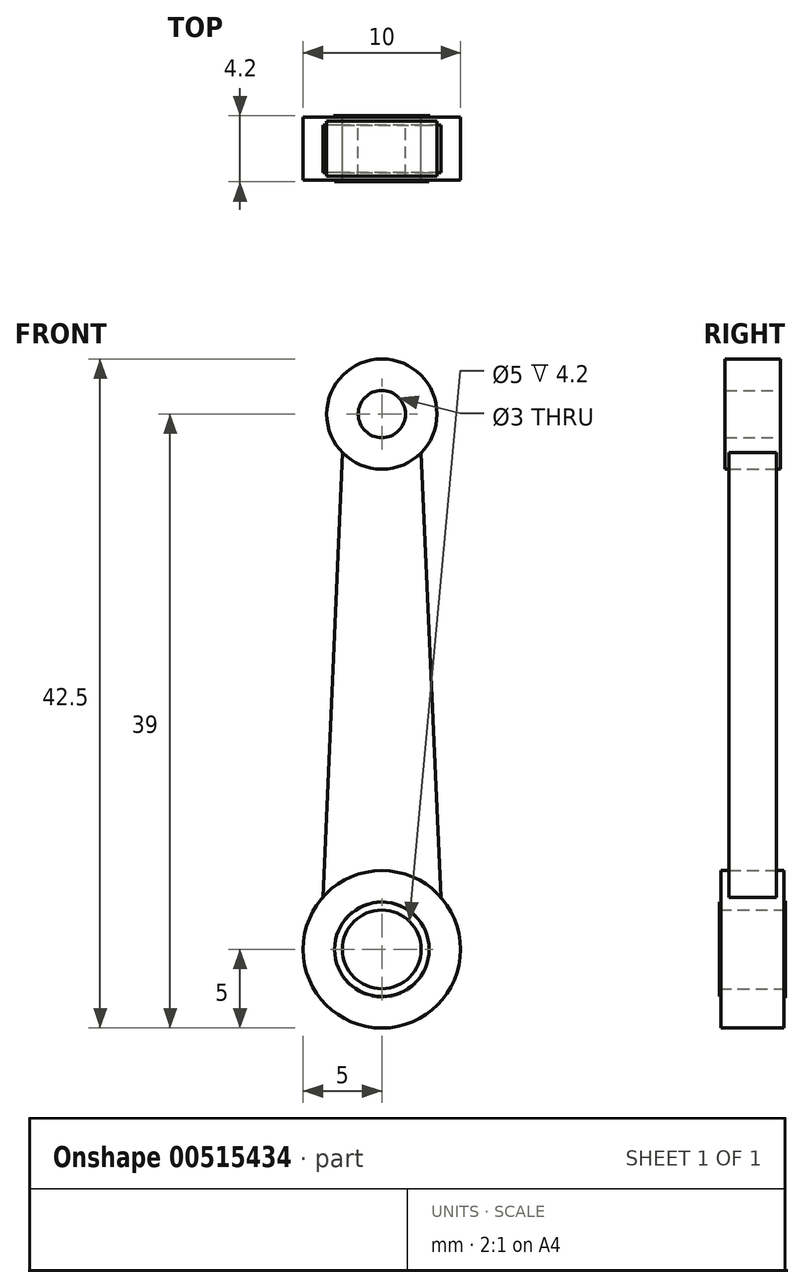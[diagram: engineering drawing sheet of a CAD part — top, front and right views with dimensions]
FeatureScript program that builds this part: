
annotation { "Feature Type Name" : "Feature", "Feature Type Description" : "" }
export const myFeature = defineFeature(function(context is Context, id is Id, definition is map)
    precondition{}
    {
        {
            var Q0;
            Q0=qCreatedBy(makeId("Front.planeOp"),FACE);
            var sketch = newSketch(context, id + "F0", { "sketchPlane" : qUnion([Q0])});
            skCircle(sketch, "E0", {"center": v(0, 0) * mm, "radius": 5 * mm});
            skCircle(sketch, "E1", {"center": v(0, 0) * mm, "radius": 3.25 * mm});
            skCircle(sketch, "E2", {"center": v(0, 0) * mm, "radius": 2.5 * mm});
            skLineSegment(sketch, "E3", {"start": v(0, 40.04) * mm, "end": v(0, -5.64) * mm, "construction": true});
            skPoint(sketch, "E4", {"position": v(0, 34) * mm});
            skCircle(sketch, "E5", {"center": v(0, 34) * mm, "radius": 3.5 * mm});
            skCircle(sketch, "E6", {"center": v(0, 34) * mm, "radius": 1.5 * mm});
            skLineSegment(sketch, "E7", {"start": v(-2.5, 31.55) * mm, "end": v(2.5, 31.55) * mm, "construction": true});
            skLineSegment(sketch, "E8", {"start": v(-3.75, 3.3) * mm, "end": v(3.75, 3.3) * mm, "construction": true});
            skPoint(sketch, "E9", {"position": v(0, 31.55) * mm});
            skPoint(sketch, "E10", {"position": v(0, 3.3) * mm});
            skLineSegment(sketch, "E11", {"start": v(-2.5, 31.55) * mm, "end": v(-3.75, 3.3) * mm});
            skLineSegment(sketch, "E12", {"start": v(2.5, 31.55) * mm, "end": v(3.75, 3.3) * mm});
            skSolve(sketch);
        }
        {
            var Q0;
            Q0=makeQuery(id+"F0.imprint","IMPRINT",FACE,{"disambiguationData":[TD([[makeQuery(id+"F0.imprint","IMPRINT",EDGE,{"derivedFrom":sQuery(id+"F0.wireOp",EDGE,"E6")}),-1.0]])]});
            extrude(context, id + "F1", {"entities" : qUnion([Q0]), "endBound" : BoundingType.SYMMETRIC, "depth" : 3.5 * mm, "offsetDistance" : 25 * mm});
        }
        {
            var Q0;
            Q0=makeQuery(id+"F0.imprint","IMPRINT",FACE,{"disambiguationData":[TD([[makeQuery(id+"F0.imprint","IMPRINT",EDGE,{"derivedFrom":sQuery(id+"F0.wireOp",EDGE,"E1")}),-1.0]])]});
            extrude(context, id + "F2", {"entities" : qUnion([Q0]), "endBound" : BoundingType.SYMMETRIC, "depth" : 4 * mm, "offsetDistance" : 25 * mm});
        }
        {
            var Q0;
            Q0=makeQuery(id+"F0.imprint","IMPRINT",FACE,{"disambiguationData":[TD([[makeQuery(id+"F0.imprint","IMPRINT",EDGE,{"derivedFrom":sQuery(id+"F0.wireOp",EDGE,"E1")}),1.0]])]});
            extrude(context, id + "F3", {"entities" : qUnion([Q0]), "operationType" : NewBodyOperationType.ADD, "endBound" : BoundingType.SYMMETRIC, "depth" : 4 * mm, "offsetDistance" : 25 * mm});
        }
        {
            var Q0;
            {var subQ0=sQuery(id+"F0.wireOp",EDGE,"E11");Q0=makeQuery(id+"F0.imprint","IMPRINT",FACE,{"disambiguationData":[TD([[makeQuery(id+"F0.imprint","IMPRINT",EDGE,{"derivedFrom":subQ0}),1.0]])]});}
            extrude(context, id + "F4", {"entities" : qUnion([Q0]), "endBound" : BoundingType.SYMMETRIC, "depth" : 3 * mm, "offsetDistance" : 25 * mm});
        }
        {
            var Q0;
            Q0=qCreatedBy(makeId("Front.planeOp"),FACE);
            var sketch = newSketch(context, id + "F5", { "sketchPlane" : qUnion([Q0])});
            skCircle(sketch, "E13", {"center": v(0, 0) * mm, "radius": 3 * mm});
            skSolve(sketch);
        }
        {
            var Q0;
            {var subQ0=sQuery(id+"F0.wireOp",EDGE,"E1");Q0=makeQuery(id+"F3.boolean.opBoolean","MERGE",FACE,{"derivedFrom":[makeQuery(id+"F2.opExtrude","CAP_FACE",FACE,{"disambiguationData":[OSD([sQuery(id+"F0.wireOp",EDGE,"E0"),subQ0])],"isStart":false}),makeQuery(id+"F3.opExtrude","CAP_FACE",FACE,{"disambiguationData":[OSD([subQ0,sQuery(id+"F0.wireOp",EDGE,"E2")])],"isStart":false})]});}
            cPlane(context, id + "F6", {"entities" : qUnion([Q0]), "cplaneType" : CPlaneType.OFFSET, "offset" : 0 * mm, "width" : 150 * mm, "height" : 150 * mm});
        }
        {
            var Q0;
            Q0=qCreatedBy(id+"F6.planeOp",FACE);
            var sketch = newSketch(context, id + "F7", { "sketchPlane" : qUnion([Q0])});
            skCircle(sketch, "E14", {"center": v(0, 0) * mm, "radius": 3 * mm});
            skSolve(sketch);
        }
        {
            var Q0;
            {var subQ0=sQuery(id+"F0.wireOp",EDGE,"E1");Q0=makeQuery(id+"F3.boolean.opBoolean","MERGE",FACE,{"derivedFrom":[makeQuery(id+"F2.opExtrude","CAP_FACE",FACE,{"disambiguationData":[OSD([sQuery(id+"F0.wireOp",EDGE,"E0"),subQ0])],"isStart":true}),makeQuery(id+"F3.opExtrude","CAP_FACE",FACE,{"disambiguationData":[OSD([subQ0,sQuery(id+"F0.wireOp",EDGE,"E2")])],"isStart":true})]});}
            cPlane(context, id + "F8", {"entities" : qUnion([Q0]), "cplaneType" : CPlaneType.OFFSET, "offset" : 0 * mm, "width" : 150 * mm, "height" : 150 * mm});
        }
        {
            var Q0;
            Q0=qCreatedBy(id+"F8.planeOp",FACE);
            var sketch = newSketch(context, id + "F9", { "sketchPlane" : qUnion([Q0])});
            skCircle(sketch, "E15", {"center": v(0, 0) * mm, "radius": 3.07 * mm});
            skSolve(sketch);
        }
        {
            var Q0;
            Q0=makeQuery(id+"F7.imprint","IMPRINT",FACE,{"disambiguationData":[TD([[makeQuery(id+"F7.imprint","IMPRINT",EDGE,{"derivedFrom":sQuery(id+"F7.wireOp",EDGE,"E14")}),1.0]])]});
            extrude(context, id + "F10", {"entities" : qUnion([Q0]), "operationType" : NewBodyOperationType.ADD, "depth" : 0.1 * mm, "offsetDistance" : 25 * mm});
        }
        {
            var Q0;
            Q0=makeQuery(id+"F9.imprint","IMPRINT",FACE,{"disambiguationData":[TD([[makeQuery(id+"F9.imprint","IMPRINT",EDGE,{"derivedFrom":sQuery(id+"F9.wireOp",EDGE,"E15")}),1.0]])]});
            extrude(context, id + "F11", {"entities" : qUnion([Q0]), "operationType" : NewBodyOperationType.ADD, "depth" : 0.1 * mm, "offsetDistance" : 25 * mm});
        }
        {
            var Q0;
            Q0=sQuery(id+"F5.wireOp",VERTEX,"E13.center");
            var Q1;
            Q1=makeQuery(id+"F2.opExtrude","SWEPT_BODY",BODY,{"disambiguationData":[OSD([sQuery(id+"F0.wireOp",EDGE,"E0"),sQuery(id+"F0.wireOp",EDGE,"E1")])]});
            hole(context, id + "F12", {"style" : HoleStyle.SIMPLE, "endStyle" : HoleEndStyle.BLIND, "oppositeDirection" : true, "holeDiameter" : 5 * mm, "holeDepth" : 5 * mm, "isTappedThrough" : true, "tappedDepth" : 12 * mm, "tapClearance" : 3, "startFromSketch" : true, "locations" : qUnion([Q0]), "scope" : qUnion([Q1])});
        }
        {
            var Q0;
            Q0=qCreatedBy(id+"F8.planeOp",FACE);
            var sketch = newSketch(context, id + "F13", { "sketchPlane" : qUnion([Q0])});
            skCircle(sketch, "E16", {"center": v(0, 0) * mm, "radius": 2.5 * mm});
            skSolve(sketch);
        }
        {
            var Q0;
            Q0=sQuery(id+"F13.wireOp",VERTEX,"E16.center");
            var Q1;
            Q1=makeQuery(id+"F2.opExtrude","SWEPT_BODY",BODY,{"disambiguationData":[OSD([sQuery(id+"F0.wireOp",EDGE,"E0"),sQuery(id+"F0.wireOp",EDGE,"E1")])]});
            hole(context, id + "F14", {"style" : HoleStyle.SIMPLE, "endStyle" : HoleEndStyle.BLIND, "oppositeDirection" : true, "holeDiameter" : 5 * mm, "holeDepth" : 5 * mm, "isTappedThrough" : true, "tappedDepth" : 12 * mm, "tapClearance" : 3, "startFromSketch" : true, "locations" : qUnion([Q0]), "scope" : qUnion([Q1])});
        }
    });
